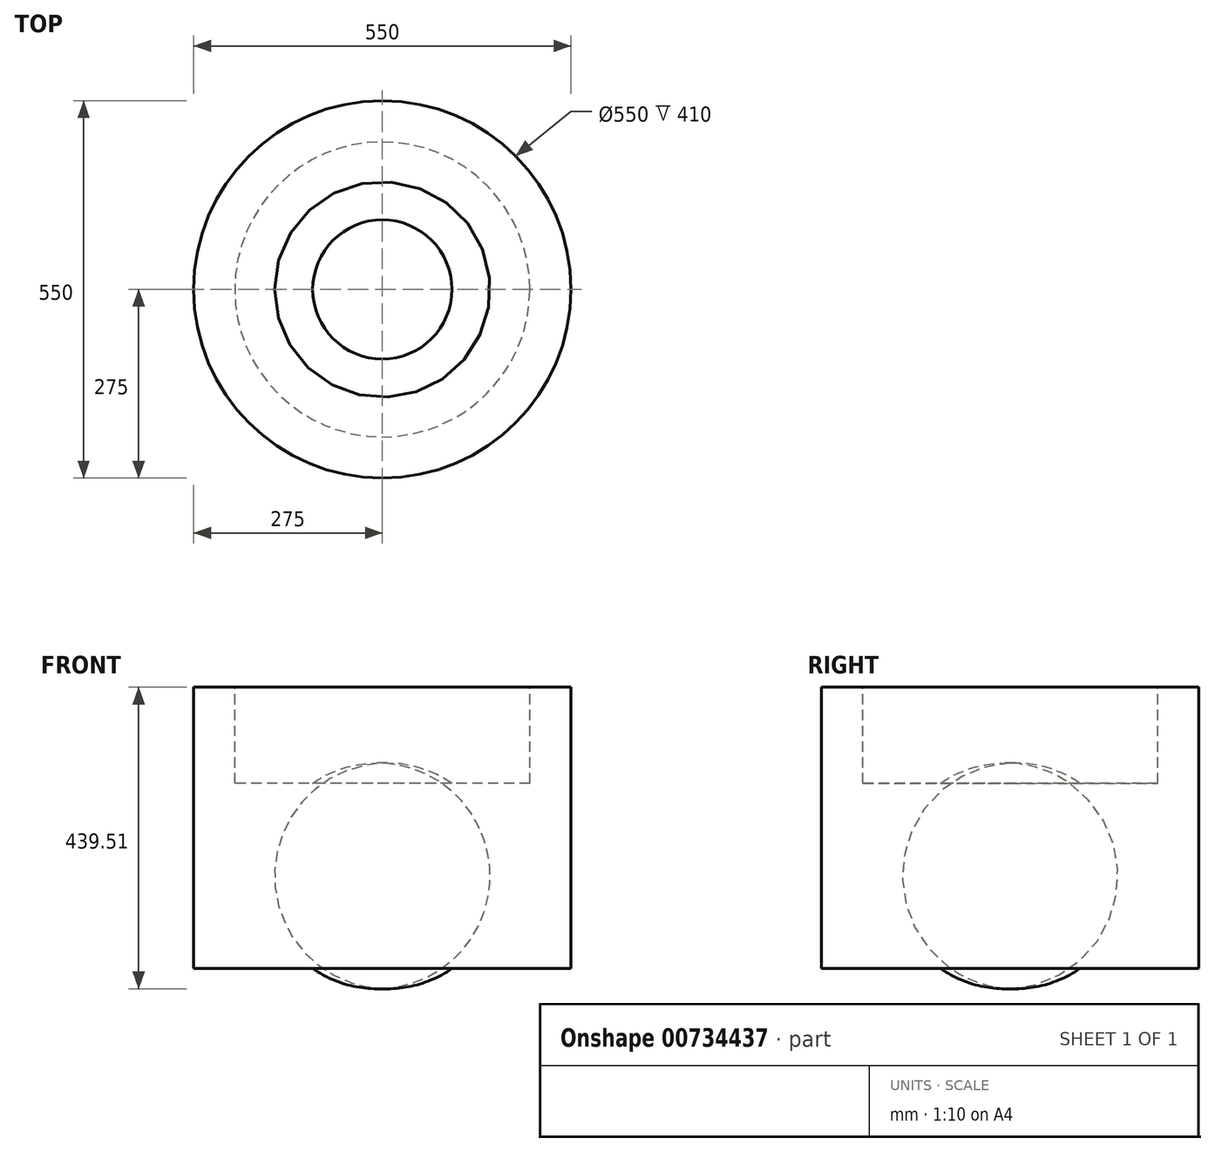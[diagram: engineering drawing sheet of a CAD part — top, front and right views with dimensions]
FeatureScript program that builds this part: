
annotation { "Feature Type Name" : "Feature", "Feature Type Description" : "" }
export const myFeature = defineFeature(function(context is Context, id is Id, definition is map)
    precondition{}
    {
        {
            var Q0;
            Q0=qCreatedBy(makeId("Right.planeOp"),FACE);
            var sketch = newSketch(context, id + "F0", { "sketchPlane" : qUnion([Q0])});
            skPoint(sketch, "E0.endSnap0", {"position": v(0, 135) * mm});
            skArc(sketch, "E1", {"start": v(0, 270) * mm, "mid": v(-70.5, 135) * mm, "end": v(0, 0) * mm});
            skPoint(sketch, "E0.end.orphan", {"position": v(-70.5, 135) * mm});
            skPoint(sketch, "E0.start.orphan", {"position": v(0, 135) * mm});
            skSolve(sketch);
        }
        {
            var Q0;
            Q0=qCreatedBy(makeId("Right.planeOp"),FACE);
            var sketch = newSketch(context, id + "F1", { "sketchPlane" : qUnion([Q0])});
            skLineSegment(sketch, "E2", {"start": v(-173.5, 0) * mm, "end": v(0, 0) * mm});
            skLineSegment(sketch, "E3", {"start": v(-173.5, 410) * mm, "end": v(-173.5, 0) * mm});
            skLineSegment(sketch, "E4", {"start": v(-113.5, 410) * mm, "end": v(-173.5, 410) * mm});
            skLineSegment(sketch, "E5", {"start": v(-113.5, 270) * mm, "end": v(-113.5, 410) * mm});
            skLineSegment(sketch, "E6", {"start": v(0, 270) * mm, "end": v(-113.5, 270) * mm});
            skPoint(sketch, "E7.orphan", {"position": v(-173.5, 135.82) * mm});
            skPoint(sketch, "E8.end.orphan", {"position": v(0, 135.82) * mm});
            skPoint(sketch, "E9.start.orphan", {"position": v(-123.5, 135.82) * mm});
            skPoint(sketch, "E10.end.orphan", {"position": v(-123.5, 150.82) * mm});
            skPoint(sketch, "E10.start.orphan", {"position": v(-173.5, 150.82) * mm});
            skSolve(sketch);
        }
        {
            var Q0;
            Q0=qCreatedBy(makeId("Right.planeOp"),FACE);
            var sketch = newSketch(context, id + "F2", { "sketchPlane" : qUnion([Q0])});
            skLineSegment(sketch, "E11", {"start": v(101.5, 0) * mm, "end": v(101.5, 250.73) * mm});
            skSolve(sketch);
        }
        {
            var Q0;
            Q0=sQuery(id+"F0.wireOp",EDGE,"E1");
            var Q1;
            Q1=sQuery(id+"F1.wireOp",EDGE,"E6");
            var Q2;
            Q2=sQuery(id+"F1.wireOp",EDGE,"E5");
            var Q3;
            Q3=sQuery(id+"F1.wireOp",EDGE,"E4");
            var Q4;
            Q4=sQuery(id+"F1.wireOp",EDGE,"E3");
            var Q5;
            Q5=sQuery(id+"F1.wireOp",EDGE,"E2");
            var Q6;
            Q6=sQuery(id+"F2.wireOp",EDGE,"E11");
            revolve(context, id + "F3", {"bodyType" : ToolBodyType.SURFACE, "surfaceOperationType" : NewSurfaceOperationType.NEW, "surfaceEntities" : qUnion([Q0, Q1, Q2, Q3, Q4, Q5]), "axis" : qUnion([Q6]), "revolveType" : RevolveType.FULL});
        }
    });
